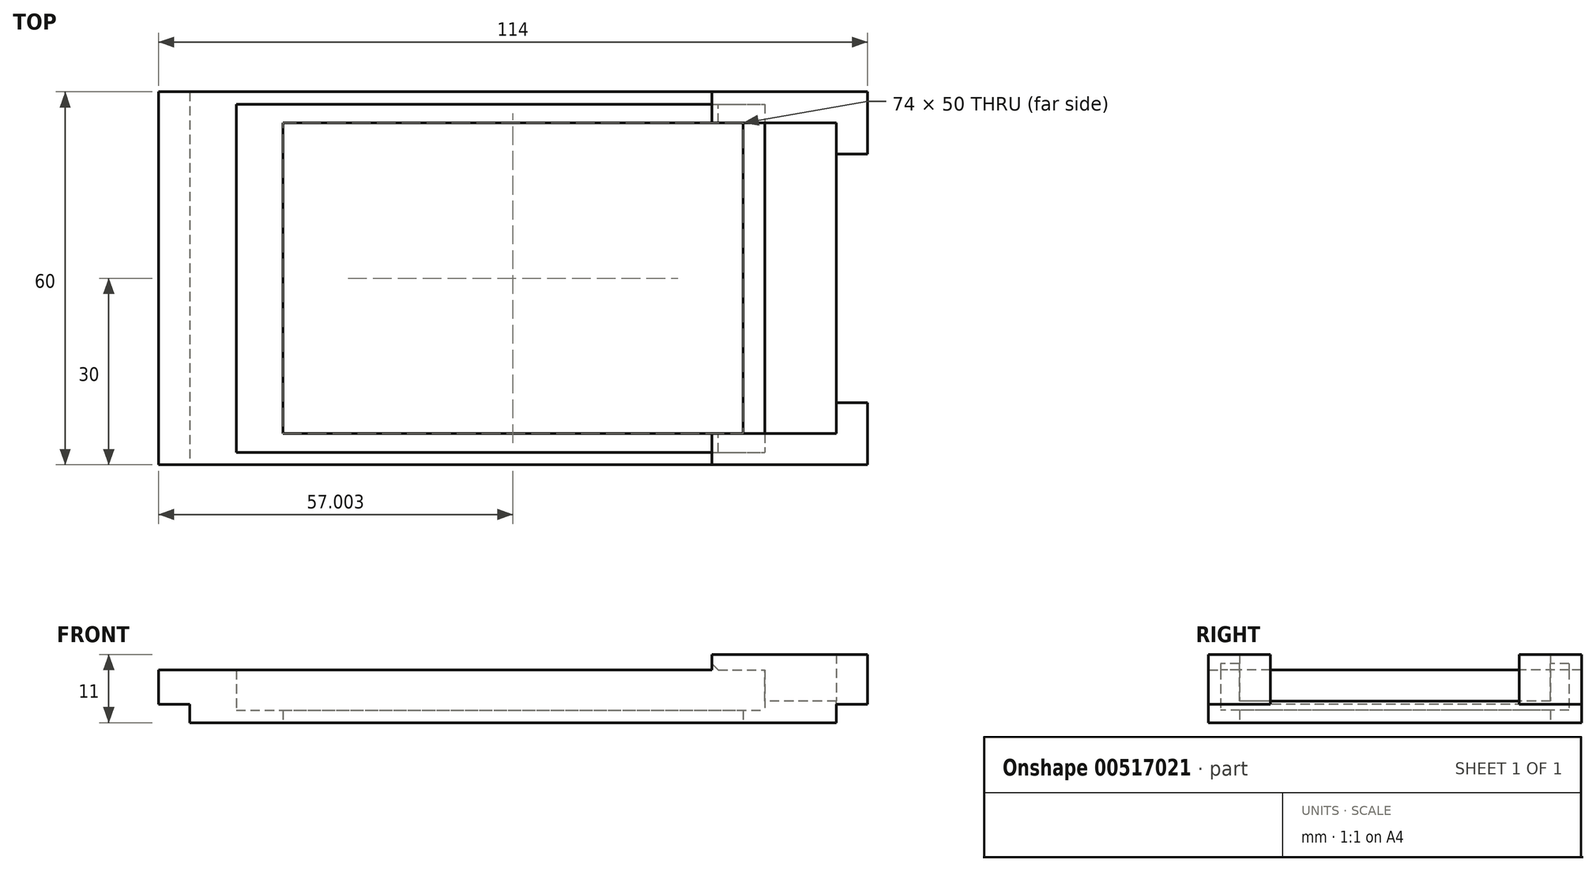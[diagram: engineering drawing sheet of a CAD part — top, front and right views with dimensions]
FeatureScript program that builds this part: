
annotation { "Feature Type Name" : "Feature", "Feature Type Description" : "" }
export const myFeature = defineFeature(function(context is Context, id is Id, definition is map)
    precondition{}
    {
        {
            var Q0;
            Q0=qCreatedBy(makeId("Top.planeOp"),FACE);
            var sketch = newSketch(context, id + "F0", { "sketchPlane" : qUnion([Q0])});
            skLineSegment(sketch, "E0.bottom", {"start": v(-50.8, 22.42) * mm, "end": v(53.2, 22.42) * mm});
            skLineSegment(sketch, "E0.top", {"start": v(-50.8, -37.58) * mm, "end": v(53.2, -37.58) * mm});
            skLineSegment(sketch, "E0.left", {"start": v(-50.8, 22.42) * mm, "end": v(-50.8, -37.58) * mm});
            skLineSegment(sketch, "E1.bottom", {"start": v(-43.3, 20.42) * mm, "end": v(41.7, 20.42) * mm});
            skLineSegment(sketch, "E1.top", {"start": v(-43.3, -35.58) * mm, "end": v(41.7, -35.58) * mm});
            skLineSegment(sketch, "E1.left", {"start": v(-43.3, 20.42) * mm, "end": v(-43.3, -35.58) * mm});
            skLineSegment(sketch, "E1.right", {"start": v(41.7, 20.42) * mm, "end": v(41.7, -35.58) * mm});
            skLineSegment(sketch, "E2.bottom", {"start": v(-35.8, 17.42) * mm, "end": v(38.2, 17.42) * mm});
            skLineSegment(sketch, "E2.top", {"start": v(-35.8, -32.58) * mm, "end": v(38.2, -32.58) * mm});
            skLineSegment(sketch, "E2.left", {"start": v(-35.8, 17.42) * mm, "end": v(-35.8, -32.58) * mm});
            skLineSegment(sketch, "E2.right", {"start": v(38.2, 17.42) * mm, "end": v(38.2, -32.58) * mm});
            skLineSegment(sketch, "E3.top", {"start": v(38.2, 17.42) * mm, "end": v(34.2, 17.42) * mm});
            skLineSegment(sketch, "E4", {"start": v(53.2, 22.42) * mm, "end": v(53.2, -37.58) * mm});
            skPoint(sketch, "E5.centerSnap0", {"position": v(-50.8, -7.58) * mm});
            skSolve(sketch);
        }
        {
            var Q0;
            Q0 = qSketchRegion(id + "F0", true);
            extrude(context, id + "F1", {"entities" : qUnion([Q0]), "depth" : 8.5 * mm, "offsetDistance" : 25 * mm});
        }
        {
            var Q0;
            Q0=makeQuery(id+"F0.imprint","IMPRINT",FACE,{"disambiguationData":[TD([[makeQuery(id+"F0.imprint","IMPRINT",EDGE,{"derivedFrom":sQuery(id+"F0.wireOp",EDGE,"E1.bottom")}),-1.0]])]});
            extrude(context, id + "F2", {"entities" : qUnion([Q0]), "operationType" : NewBodyOperationType.ADD, "depth" : 2 * mm, "offsetDistance" : 25 * mm});
        }
        {
            var Q0;
            Q0=makeQuery(id+"F1.opExtrude","CAP_FACE",FACE,{"disambiguationData":[OSD([sQuery(id+"F0.wireOp",EDGE,"E0.bottom"),sQuery(id+"F0.wireOp",EDGE,"E0.top"),sQuery(id+"F0.wireOp",EDGE,"E0.left"),sQuery(id+"F0.wireOp",EDGE,"E1.bottom"),sQuery(id+"F0.wireOp",EDGE,"E1.top"),sQuery(id+"F0.wireOp",EDGE,"E1.left"),sQuery(id+"F0.wireOp",EDGE,"E1.right"),sQuery(id+"F0.wireOp",EDGE,"E4")])],"isStart":false});
            var sketch = newSketch(context, id + "F3", { "sketchPlane" : qUnion([Q0])});
            skLineSegment(sketch, "E6.bottom", {"start": v(53.2, -37.58) * mm, "end": v(33.2, -37.58) * mm});
            skLineSegment(sketch, "E6.top", {"start": v(53.2, -32.58) * mm, "end": v(33.2, -32.58) * mm});
            skLineSegment(sketch, "E6.left", {"start": v(53.2, -37.58) * mm, "end": v(53.2, -32.58) * mm});
            skLineSegment(sketch, "E6.right", {"start": v(33.2, -37.58) * mm, "end": v(33.2, -32.58) * mm});
            skLineSegment(sketch, "E7.bottom", {"start": v(53.2, 22.42) * mm, "end": v(33.2, 22.42) * mm});
            skLineSegment(sketch, "E7.top", {"start": v(53.2, 17.42) * mm, "end": v(33.2, 17.42) * mm});
            skLineSegment(sketch, "E7.left", {"start": v(53.2, 22.42) * mm, "end": v(53.2, 17.42) * mm});
            skLineSegment(sketch, "E7.right", {"start": v(33.2, 22.42) * mm, "end": v(33.2, 17.42) * mm});
            skSolve(sketch);
        }
        {
            var Q0;
            {var subQ0=sQuery(id+"F3.wireOp",EDGE,"E6.right");var subQ1=sQuery(id+"F3.wireOp",EDGE,"E6.top");var subQ2=makeQuery(id+"F3.imprint","INTERSECT",VERTEX,{"derivedFrom":[subQ1,subQ0]});Q0=makeQuery(id+"F3.imprint","IMPRINT",FACE,{"disambiguationData":[TD([[makeQuery(id+"F3.imprint","IMPRINT",EDGE,{"disambiguationData":[TD([[subQ2,1.0]])],"derivedFrom":subQ1}),1.0]])]});}
            var Q1;
            {var subQ0=sQuery(id+"F3.wireOp",EDGE,"E7.right");var subQ1=sQuery(id+"F3.wireOp",EDGE,"E7.top");var subQ2=makeQuery(id+"F3.imprint","INTERSECT",VERTEX,{"derivedFrom":[subQ1,subQ0]});Q1=makeQuery(id+"F3.imprint","IMPRINT",FACE,{"disambiguationData":[TD([[makeQuery(id+"F3.imprint","IMPRINT",EDGE,{"disambiguationData":[TD([[subQ2,1.0]])],"derivedFrom":subQ1}),-1.0]])]});}
            var Q2;
            {var subQ1=sQuery(id+"F3.wireOp",EDGE,"E6.bottom");Q2=makeQuery(id+"F3.imprint","IMPRINT",FACE,{"disambiguationData":[TD([[makeQuery(id+"F3.imprint","IMPRINT",EDGE,{"derivedFrom":subQ1}),1.0]])]});}
            var Q3;
            {var subQ1=sQuery(id+"F3.wireOp",EDGE,"E7.bottom");Q3=makeQuery(id+"F3.imprint","IMPRINT",FACE,{"disambiguationData":[TD([[makeQuery(id+"F3.imprint","IMPRINT",EDGE,{"derivedFrom":subQ1}),-1.0]])]});}
            extrude(context, id + "F4", {"entities" : qUnion([Q0, Q1, Q2, Q3]), "operationType" : NewBodyOperationType.ADD, "depth" : 2.5 * mm, "offsetDistance" : 25 * mm});
        }
        {
            var Q0;
            {var subQ0=sQuery(id+"F3.wireOp",EDGE,"E7.right");Q0=makeQuery(id+"F4.boolean.opBoolean","SPLIT",EDGE,{"disambiguationData":[topologyDisambiguationEdgeConnected([makeQuery(id+"F4.opExtrude","CAP_FACE",FACE,{"disambiguationData":[OSD([sQuery(id+"F3.wireOp",EDGE,"E7.bottom"),sQuery(id+"F3.wireOp",EDGE,"E7.top"),sQuery(id+"F3.wireOp",EDGE,"E7.left"),subQ0])],"isStart":true})])],"derivedFrom":makeQuery(id+"F4.opExtrude","CAP_EDGE",EDGE,{"disambiguationData":[OSD([subQ0])],"isStart":true})});}
            var Q1;
            {var subQ0=sQuery(id+"F3.wireOp",EDGE,"E6.right");Q1=makeQuery(id+"F4.boolean.opBoolean","SPLIT",EDGE,{"disambiguationData":[topologyDisambiguationEdgeConnected([makeQuery(id+"F4.opExtrude","CAP_FACE",FACE,{"disambiguationData":[OSD([sQuery(id+"F3.wireOp",EDGE,"E6.bottom"),sQuery(id+"F3.wireOp",EDGE,"E6.top"),sQuery(id+"F3.wireOp",EDGE,"E6.left"),subQ0])],"isStart":true})])],"derivedFrom":makeQuery(id+"F4.opExtrude","CAP_EDGE",EDGE,{"disambiguationData":[OSD([subQ0])],"isStart":true})});}
            chamfer(context, id + "F5", {"entities" : qUnion([Q0, Q1]), "width" : 1 * mm, "tangentPropagation" : true});
        }
        {
            var Q0;
            {var subQ2=sQuery(id+"F0.wireOp",EDGE,"E4");var subQ3=sQuery(id+"F0.wireOp",EDGE,"E1.right");Q0=makeQuery(id+"F4.boolean.opBoolean","SPLIT",FACE,{"disambiguationData":[TD([makeQuery(id+"F1.opExtrude","SWEPT_FACE",FACE,{"disambiguationData":[OSD([subQ3])]})])],"derivedFrom":makeQuery(id+"F1.opExtrude","CAP_FACE",FACE,{"disambiguationData":[OSD([sQuery(id+"F0.wireOp",EDGE,"E0.bottom"),sQuery(id+"F0.wireOp",EDGE,"E0.top"),sQuery(id+"F0.wireOp",EDGE,"E0.left"),sQuery(id+"F0.wireOp",EDGE,"E1.bottom"),sQuery(id+"F0.wireOp",EDGE,"E1.top"),sQuery(id+"F0.wireOp",EDGE,"E1.left"),subQ3,subQ2])],"isStart":false})});}
            extrude(context, id + "F6", {"entities" : qUnion([Q0]), "operationType" : NewBodyOperationType.REMOVE, "oppositeDirection" : true, "depth" : 5 * mm, "offsetDistance" : 25 * mm});
        }
        {
            var Q0;
            Q0=makeQuery(id+"F4.opExtrude","CAP_FACE",FACE,{"disambiguationData":[OSD([sQuery(id+"F3.wireOp",EDGE,"E7.bottom"),sQuery(id+"F3.wireOp",EDGE,"E7.top"),sQuery(id+"F3.wireOp",EDGE,"E7.left"),sQuery(id+"F3.wireOp",EDGE,"E7.right")])],"isStart":false});
            var sketch = newSketch(context, id + "F7", { "sketchPlane" : qUnion([Q0])});
            skLineSegment(sketch, "E8.bottom", {"start": v(53.2, 12.42) * mm, "end": v(58.2, 12.42) * mm});
            skLineSegment(sketch, "E8.top", {"start": v(53.2, 22.42) * mm, "end": v(58.2, 22.42) * mm});
            skLineSegment(sketch, "E8.left", {"start": v(53.2, 12.42) * mm, "end": v(53.2, 22.42) * mm});
            skLineSegment(sketch, "E8.right", {"start": v(58.2, 12.42) * mm, "end": v(58.2, 22.42) * mm});
            skLineSegment(sketch, "E9.bottom", {"start": v(53.2, -27.58) * mm, "end": v(58.2, -27.58) * mm});
            skLineSegment(sketch, "E9.top", {"start": v(53.2, -37.58) * mm, "end": v(58.2, -37.58) * mm});
            skLineSegment(sketch, "E9.left", {"start": v(53.2, -27.58) * mm, "end": v(53.2, -37.58) * mm});
            skLineSegment(sketch, "E9.right", {"start": v(58.2, -27.58) * mm, "end": v(58.2, -37.58) * mm});
            skSolve(sketch);
        }
        {
            var Q0;
            Q0=makeQuery(id+"F7.imprint","IMPRINT",FACE,{"disambiguationData":[TD([[makeQuery(id+"F7.imprint","IMPRINT",EDGE,{"derivedFrom":sQuery(id+"F7.wireOp",EDGE,"E8.bottom")}),1.0]])]});
            var Q1;
            Q1=makeQuery(id+"F7.imprint","IMPRINT",FACE,{"disambiguationData":[TD([[makeQuery(id+"F7.imprint","IMPRINT",EDGE,{"derivedFrom":sQuery(id+"F7.wireOp",EDGE,"E9.bottom")}),-1.0]])]});
            extrude(context, id + "F8", {"entities" : qUnion([Q0, Q1]), "operationType" : NewBodyOperationType.ADD, "oppositeDirection" : true, "depth" : 8 * mm, "offsetDistance" : 25 * mm});
        }
        {
            var Q0;
            {var subQ2=sQuery(id+"F0.wireOp",EDGE,"E0.bottom");var subQ3=sQuery(id+"F0.wireOp",EDGE,"E1.left");var subQ4=sQuery(id+"F0.wireOp",EDGE,"E1.top");var subQ7=sQuery(id+"F0.wireOp",EDGE,"E1.bottom");var subQ8=sQuery(id+"F0.wireOp",EDGE,"E0.left");var subQ9=sQuery(id+"F0.wireOp",EDGE,"E0.top");Q0=makeQuery(id+"F4.boolean.opBoolean","SPLIT",FACE,{"disambiguationData":[TD([makeQuery(id+"F1.opExtrude","SWEPT_FACE",FACE,{"disambiguationData":[OSD([subQ2])]})])],"derivedFrom":makeQuery(id+"F1.opExtrude","CAP_FACE",FACE,{"disambiguationData":[OSD([subQ2,subQ9,subQ8,subQ7,subQ4,subQ3,sQuery(id+"F0.wireOp",EDGE,"E1.right"),sQuery(id+"F0.wireOp",EDGE,"E4")])],"isStart":false})});}
            var sketch = newSketch(context, id + "F9", { "sketchPlane" : qUnion([Q0])});
            skLineSegment(sketch, "E10.bottom", {"start": v(-50.8, 22.42) * mm, "end": v(-55.8, 22.42) * mm});
            skLineSegment(sketch, "E10.top", {"start": v(-50.8, -37.58) * mm, "end": v(-55.8, -37.58) * mm});
            skLineSegment(sketch, "E10.left", {"start": v(-50.8, 22.42) * mm, "end": v(-50.8, -37.58) * mm});
            skLineSegment(sketch, "E10.right", {"start": v(-55.8, 22.42) * mm, "end": v(-55.8, -37.58) * mm});
            skSolve(sketch);
        }
        {
            var Q0;
            Q0 = qSketchRegion(id + "F9", true);
            extrude(context, id + "F10", {"entities" : qUnion([Q0]), "operationType" : NewBodyOperationType.ADD, "oppositeDirection" : true, "depth" : 5.5 * mm, "offsetDistance" : 25 * mm});
        }
    });
